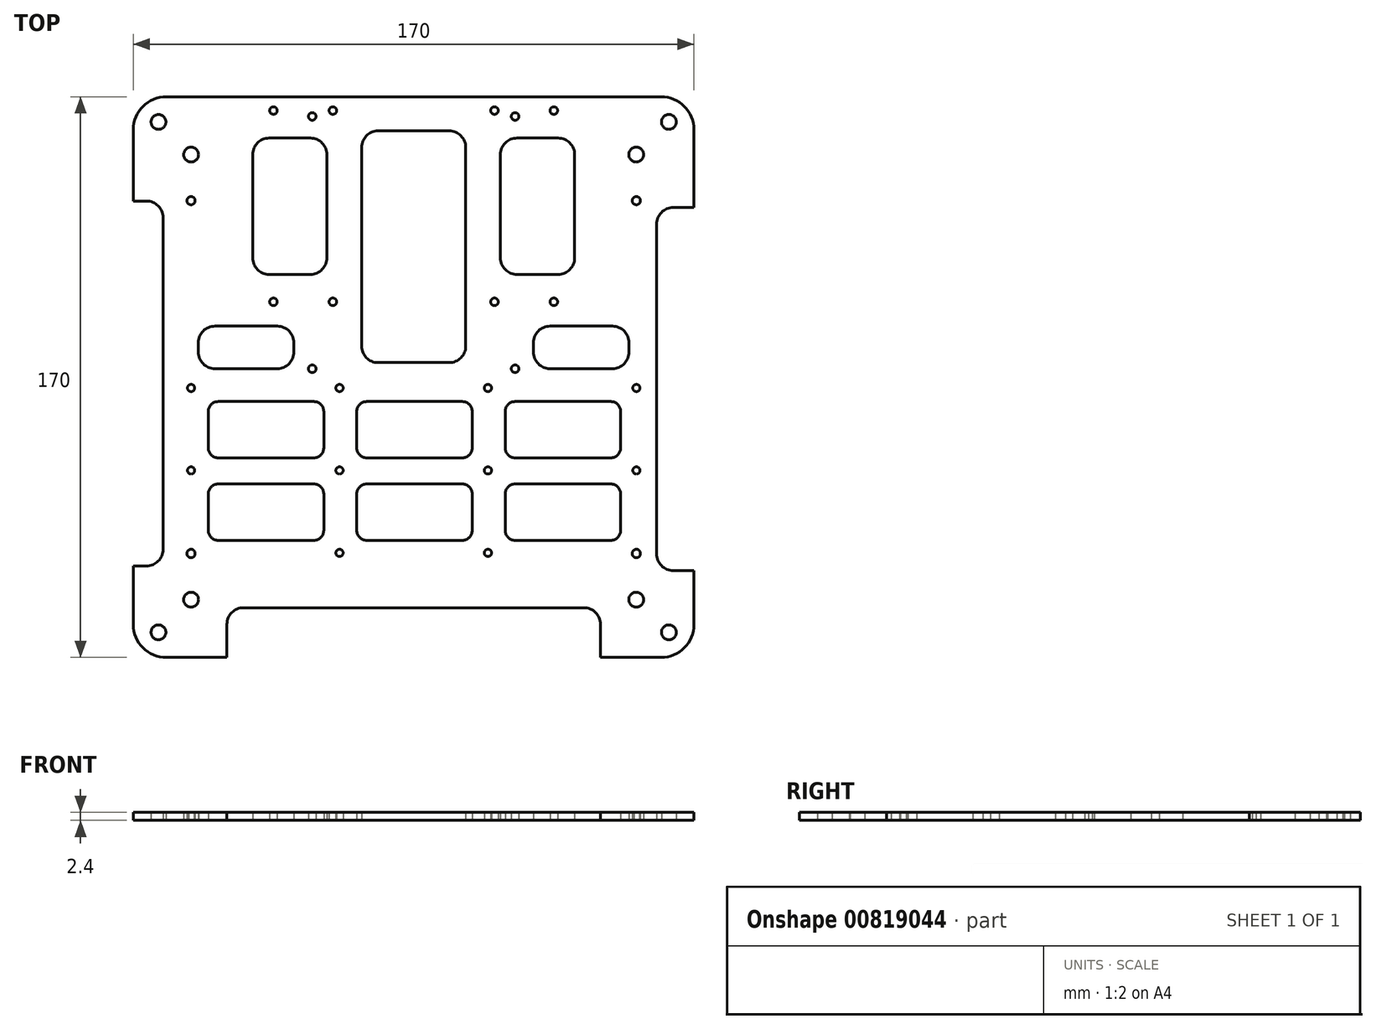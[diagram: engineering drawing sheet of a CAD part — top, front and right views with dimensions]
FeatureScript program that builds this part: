
annotation { "Feature Type Name" : "Feature", "Feature Type Description" : "" }
export const myFeature = defineFeature(function(context is Context, id is Id, definition is map)
    precondition{}
    {
        {
            var Q0;
            Q0=qCreatedBy(makeId("Top.planeOp"),FACE);
            var sketch = newSketch(context, id + "F0", { "sketchPlane" : qUnion([Q0])});
            skLineSegment(sketch, "E0.bottom", {"start": v(-100, -100) * mm, "end": v(100, -100) * mm, "construction": true});
            skLineSegment(sketch, "E0.top", {"start": v(-100, 100) * mm, "end": v(100, 100) * mm, "construction": true});
            skLineSegment(sketch, "E0.left", {"start": v(-100, -100) * mm, "end": v(-100, 100) * mm, "construction": true});
            skLineSegment(sketch, "E0.right", {"start": v(100, -100) * mm, "end": v(100, 100) * mm, "construction": true});
            skPoint(sketch, "E0.middle", {"position": v(0, 0) * mm});
            skCircle(sketch, "E1", {"center": v(-100, 100) * mm, "radius": 2.5 * mm, "construction": true});
            skCircle(sketch, "E2", {"center": v(100, 100) * mm, "radius": 2.5 * mm, "construction": true});
            skCircle(sketch, "E3", {"center": v(100, -100) * mm, "radius": 2.5 * mm, "construction": true});
            skCircle(sketch, "E4", {"center": v(-100, -100) * mm, "radius": 2.5 * mm, "construction": true});
            skLineSegment(sketch, "E5", {"start": v(-100, 100) * mm, "end": v(-77.37, 77.37) * mm, "construction": true});
            skLineSegment(sketch, "E6", {"start": v(-77.37, 77.37) * mm, "end": v(-67.47, 67.47) * mm, "construction": true});
            skCircle(sketch, "E7", {"center": v(-77.37, 77.37) * mm, "radius": 2.25 * mm});
            skCircle(sketch, "E8", {"center": v(-67.47, 67.47) * mm, "radius": 2.25 * mm});
            skLineSegment(sketch, "E9.bottom", {"start": v(-85, 85) * mm, "end": v(85, 85) * mm});
            skLineSegment(sketch, "E9.top", {"start": v(-85, -85) * mm, "end": v(85, -85) * mm});
            skLineSegment(sketch, "E9.left", {"start": v(-85, 85) * mm, "end": v(-85, -85) * mm});
            skLineSegment(sketch, "E9.right", {"start": v(85, 85) * mm, "end": v(85, -85) * mm});
            skLineSegment(sketch, "E10.bottom", {"start": v(-30.75, 2.54) * mm, "end": v(30.75, 2.54) * mm, "construction": true});
            skLineSegment(sketch, "E10.top", {"start": v(-30.75, 79.04) * mm, "end": v(30.75, 79.04) * mm, "construction": true});
            skLineSegment(sketch, "E10.left", {"start": v(-30.75, 2.54) * mm, "end": v(-30.75, 79.04) * mm, "construction": true});
            skLineSegment(sketch, "E10.right", {"start": v(30.75, 2.54) * mm, "end": v(30.75, 79.04) * mm, "construction": true});
            skPoint(sketch, "E10.middle", {"position": v(0, 40.8) * mm});
            skLineSegment(sketch, "E11.bottom", {"start": v(-35, -9.2) * mm, "end": v(35, -9.2) * mm, "construction": true});
            skLineSegment(sketch, "E11.top", {"start": v(-35, 90.8) * mm, "end": v(35, 90.8) * mm, "construction": true});
            skLineSegment(sketch, "E11.left", {"start": v(-35, -9.2) * mm, "end": v(-35, 90.8) * mm, "construction": true});
            skLineSegment(sketch, "E11.right", {"start": v(35, -9.2) * mm, "end": v(35, 90.8) * mm, "construction": true});
            skLineSegment(sketch, "E12.bottom", {"start": v(24.5, 22.83) * mm, "end": v(-24.5, 22.83) * mm, "construction": true});
            skLineSegment(sketch, "E12.top", {"start": v(24.5, 80.83) * mm, "end": v(-24.5, 80.83) * mm, "construction": true});
            skLineSegment(sketch, "E12.left", {"start": v(24.5, 22.83) * mm, "end": v(24.5, 80.83) * mm, "construction": true});
            skLineSegment(sketch, "E12.right", {"start": v(-24.5, 22.83) * mm, "end": v(-24.5, 80.83) * mm, "construction": true});
            skPoint(sketch, "E12.middle", {"position": v(0, 51.83) * mm});
            skLineSegment(sketch, "E13.bottom", {"start": v(28, 96.83) * mm, "end": v(-28, 96.83) * mm, "construction": true});
            skLineSegment(sketch, "E13.top", {"start": v(28, 6.83) * mm, "end": v(-28, 6.83) * mm, "construction": true});
            skLineSegment(sketch, "E13.left", {"start": v(28, 96.83) * mm, "end": v(28, 6.83) * mm, "construction": true});
            skLineSegment(sketch, "E13.right", {"start": v(-28, 96.83) * mm, "end": v(-28, 6.83) * mm, "construction": true});
            skLineSegment(sketch, "E14", {"start": v(0, 0) * mm, "end": v(0, 19) * mm, "construction": true});
            skLineSegment(sketch, "E15", {"start": v(0, 0) * mm, "end": v(16.24, 0) * mm, "construction": true});
            skCircle(sketch, "E16.MirrorC", {"center": v(77.37, 77.37) * mm, "radius": 2.25 * mm});
            skCircle(sketch, "E17.MirrorC", {"center": v(67.47, 67.47) * mm, "radius": 2.25 * mm});
            skCircle(sketch, "E18.MirrorC", {"center": v(-67.47, -67.47) * mm, "radius": 2.25 * mm});
            skCircle(sketch, "E19.MirrorC", {"center": v(-77.37, -77.37) * mm, "radius": 2.25 * mm});
            skCircle(sketch, "E20.MirrorC", {"center": v(77.37, -77.37) * mm, "radius": 2.25 * mm});
            skCircle(sketch, "E21.MirrorC", {"center": v(67.47, -67.47) * mm, "radius": 2.25 * mm});
            skCircle(sketch, "E22", {"center": v(-24.5, 80.83) * mm, "radius": 1.15 * mm});
            skCircle(sketch, "E23", {"center": v(24.5, 80.83) * mm, "radius": 1.15 * mm});
            skCircle(sketch, "E24", {"center": v(24.5, 22.83) * mm, "radius": 1.15 * mm});
            skCircle(sketch, "E25", {"center": v(-24.5, 22.83) * mm, "radius": 1.15 * mm});
            skCircle(sketch, "E26", {"center": v(-30.75, 79.04) * mm, "radius": 1.15 * mm});
            skCircle(sketch, "E27", {"center": v(30.75, 79.04) * mm, "radius": 1.15 * mm});
            skCircle(sketch, "E28", {"center": v(30.75, 2.54) * mm, "radius": 1.15 * mm});
            skCircle(sketch, "E29", {"center": v(-30.75, 2.54) * mm, "radius": 1.15 * mm});
            skLineSegment(sketch, "E30.bottom", {"start": v(-67.5, 53.5) * mm, "end": v(67.5, 53.5) * mm, "construction": true});
            skLineSegment(sketch, "E30.top", {"start": v(-67.5, -53.5) * mm, "end": v(67.5, -53.5) * mm, "construction": true});
            skLineSegment(sketch, "E30.left", {"start": v(-67.5, 53.5) * mm, "end": v(-67.5, -53.5) * mm, "construction": true});
            skLineSegment(sketch, "E30.right", {"start": v(67.5, 53.5) * mm, "end": v(67.5, -53.5) * mm, "construction": true});
            skCircle(sketch, "E31", {"center": v(-67.5, 53.5) * mm, "radius": 1.25 * mm});
            skCircle(sketch, "E32", {"center": v(67.5, 53.5) * mm, "radius": 1.25 * mm});
            skCircle(sketch, "E33", {"center": v(67.5, -53.5) * mm, "radius": 1.25 * mm});
            skCircle(sketch, "E34", {"center": v(-67.5, -53.5) * mm, "radius": 1.25 * mm});
            skLineSegment(sketch, "E35.bottom", {"start": v(-42.5, 22.83) * mm, "end": v(42.5, 22.83) * mm, "construction": true});
            skLineSegment(sketch, "E35.top", {"start": v(-42.5, 80.83) * mm, "end": v(42.5, 80.83) * mm, "construction": true});
            skLineSegment(sketch, "E35.left", {"start": v(-42.5, 22.83) * mm, "end": v(-42.5, 80.83) * mm, "construction": true});
            skLineSegment(sketch, "E35.right", {"start": v(42.5, 22.83) * mm, "end": v(42.5, 80.83) * mm, "construction": true});
            skCircle(sketch, "E36", {"center": v(-42.5, 80.83) * mm, "radius": 1.15 * mm});
            skCircle(sketch, "E37", {"center": v(-42.5, 22.83) * mm, "radius": 1.15 * mm});
            skCircle(sketch, "E38", {"center": v(42.5, 22.83) * mm, "radius": 1.15 * mm});
            skCircle(sketch, "E39", {"center": v(42.5, 80.83) * mm, "radius": 1.15 * mm});
            skSolve(sketch);
        }
        {
            var Q0;
            Q0=qSketchRegion(id+"F0",true);
            extrude(context, id + "F1", {"entities" : qUnion([Q0]), "depth" : 2.4 * mm, "offsetDistance" : 25 * mm});
        }
        {
            var Q0;
            Q0=makeQuery(id+"F1.opExtrude","SWEPT_EDGE",EDGE,{"disambiguationData":[OSD([sQuery(id+"F0.wireOp",EDGE,"E9.bottom"),sQuery(id+"F0.wireOp",EDGE,"E9.left")])]});
            var Q1;
            Q1=makeQuery(id+"F1.opExtrude","SWEPT_EDGE",EDGE,{"disambiguationData":[OSD([sQuery(id+"F0.wireOp",EDGE,"E9.bottom"),sQuery(id+"F0.wireOp",EDGE,"E9.right")])]});
            var Q2;
            Q2=makeQuery(id+"F1.opExtrude","SWEPT_EDGE",EDGE,{"disambiguationData":[OSD([sQuery(id+"F0.wireOp",EDGE,"E9.top"),sQuery(id+"F0.wireOp",EDGE,"E9.right")])]});
            var Q3;
            Q3=makeQuery(id+"F1.opExtrude","SWEPT_EDGE",EDGE,{"disambiguationData":[OSD([sQuery(id+"F0.wireOp",EDGE,"E9.top"),sQuery(id+"F0.wireOp",EDGE,"E9.left")])]});
            fillet(context, id + "F2", {"entities" : qUnion([Q0, Q1, Q2, Q3]), "radius" : 10 * mm, "tangentPropagation" : true, "allowEdgeOverflow" : false});
        }
        {
            var Q0;
            Q0=qCreatedBy(makeId("Top.planeOp"),FACE);
            var sketch = newSketch(context, id + "F3", { "sketchPlane" : qUnion([Q0])});
            skCircle(sketch, "E40", {"center": v(-67.48, -53.3) * mm, "radius": 1.1 * mm});
            skLineSegment(sketch, "E41", {"start": v(-67.48, -53.3) * mm, "end": v(-67.48, -28.3) * mm, "construction": true});
            skCircle(sketch, "E42", {"center": v(-67.48, -28.3) * mm, "radius": 1.1 * mm});
            skLineSegment(sketch, "E43.bottom", {"start": v(-59.25, -32.4) * mm, "end": v(-30.25, -32.4) * mm});
            skLineSegment(sketch, "E43.top", {"start": v(-59.25, -49.48) * mm, "end": v(-30.25, -49.48) * mm});
            skLineSegment(sketch, "E43.left", {"start": v(-62.25, -35.4) * mm, "end": v(-62.25, -46.48) * mm});
            skLineSegment(sketch, "E43.right", {"start": v(-27.25, -35.4) * mm, "end": v(-27.25, -46.48) * mm});
            skPoint(sketch, "E44.visualSharp", {"position": v(-62.25, -32.4) * mm});
            skArc(sketch, "E44.filletArc", {"start": v(-59.25, -32.4) * mm, "mid": v(-61.37, -33.29) * mm, "end": v(-62.25, -35.4) * mm});
            skPoint(sketch, "E45.visualSharp", {"position": v(-27.25, -32.4) * mm});
            skArc(sketch, "E45.filletArc", {"start": v(-27.25, -35.4) * mm, "mid": v(-28.13, -33.29) * mm, "end": v(-30.25, -32.4) * mm});
            skPoint(sketch, "E46.visualSharp", {"position": v(-27.25, -49.48) * mm});
            skArc(sketch, "E46.filletArc", {"start": v(-30.25, -49.48) * mm, "mid": v(-28.13, -48.6) * mm, "end": v(-27.25, -46.48) * mm});
            skPoint(sketch, "E47.visualSharp", {"position": v(-62.25, -49.48) * mm});
            skArc(sketch, "E47.filletArc", {"start": v(-62.25, -46.48) * mm, "mid": v(-61.37, -48.6) * mm, "end": v(-59.25, -49.48) * mm});
            skLineSegment(sketch, "E48.0.1.0", {"start": v(-27.25, -10.4) * mm, "end": v(-27.25, -21.48) * mm});
            skLineSegment(sketch, "E48.0.1.1", {"start": v(-59.25, -7.4) * mm, "end": v(-30.25, -7.4) * mm});
            skLineSegment(sketch, "E48.0.1.2", {"start": v(-67.48, -28.3) * mm, "end": v(-67.48, -3.3) * mm, "construction": true});
            skLineSegment(sketch, "E48.0.1.3", {"start": v(-62.25, -10.4) * mm, "end": v(-62.25, -21.48) * mm});
            skLineSegment(sketch, "E48.0.1.4", {"start": v(-59.25, -24.48) * mm, "end": v(-30.25, -24.48) * mm});
            skPoint(sketch, "E48.0.1.5", {"position": v(-62.25, -24.48) * mm});
            skPoint(sketch, "E48.0.1.6", {"position": v(-27.25, -24.48) * mm});
            skPoint(sketch, "E48.0.1.7", {"position": v(-27.25, -7.4) * mm});
            skPoint(sketch, "E48.0.1.8", {"position": v(-62.25, -7.4) * mm});
            skArc(sketch, "E48.0.1.9", {"start": v(-59.25, -7.4) * mm, "mid": v(-61.37, -8.29) * mm, "end": v(-62.25, -10.4) * mm});
            skArc(sketch, "E48.0.1.10", {"start": v(-30.25, -24.48) * mm, "mid": v(-28.13, -23.6) * mm, "end": v(-27.25, -21.48) * mm});
            skArc(sketch, "E48.0.1.11", {"start": v(-62.25, -21.48) * mm, "mid": v(-61.37, -23.6) * mm, "end": v(-59.25, -24.48) * mm});
            skCircle(sketch, "E48.0.1.12", {"center": v(-67.48, -3.3) * mm, "radius": 1.1 * mm});
            skArc(sketch, "E48.0.1.14", {"start": v(-27.25, -10.4) * mm, "mid": v(-28.13, -8.29) * mm, "end": v(-30.25, -7.4) * mm});
            skLineSegment(sketch, "E48.1.0.0", {"start": v(17.75, -35.4) * mm, "end": v(17.75, -46.48) * mm});
            skLineSegment(sketch, "E48.1.0.1", {"start": v(-14.25, -32.4) * mm, "end": v(14.75, -32.4) * mm});
            skLineSegment(sketch, "E48.1.0.2", {"start": v(-22.48, -53.3) * mm, "end": v(-22.48, -28.3) * mm, "construction": true});
            skLineSegment(sketch, "E48.1.0.3", {"start": v(-17.25, -35.4) * mm, "end": v(-17.25, -46.48) * mm});
            skLineSegment(sketch, "E48.1.0.4", {"start": v(-14.25, -49.48) * mm, "end": v(14.75, -49.48) * mm});
            skPoint(sketch, "E48.1.0.5", {"position": v(-17.25, -49.48) * mm});
            skPoint(sketch, "E48.1.0.6", {"position": v(17.75, -49.48) * mm});
            skPoint(sketch, "E48.1.0.7", {"position": v(17.75, -32.4) * mm});
            skPoint(sketch, "E48.1.0.8", {"position": v(-17.25, -32.4) * mm});
            skArc(sketch, "E48.1.0.9", {"start": v(-14.25, -32.4) * mm, "mid": v(-16.37, -33.29) * mm, "end": v(-17.25, -35.4) * mm});
            skArc(sketch, "E48.1.0.10", {"start": v(14.75, -49.48) * mm, "mid": v(16.87, -48.6) * mm, "end": v(17.75, -46.48) * mm});
            skArc(sketch, "E48.1.0.11", {"start": v(-17.25, -46.48) * mm, "mid": v(-16.37, -48.6) * mm, "end": v(-14.25, -49.48) * mm});
            skCircle(sketch, "E48.1.0.12", {"center": v(-22.48, -28.3) * mm, "radius": 1.1 * mm});
            skCircle(sketch, "E48.1.0.13", {"center": v(-22.48, -53.3) * mm, "radius": 1.1 * mm});
            skArc(sketch, "E48.1.0.14", {"start": v(17.75, -35.4) * mm, "mid": v(16.87, -33.29) * mm, "end": v(14.75, -32.4) * mm});
            skLineSegment(sketch, "E48.1.1.0", {"start": v(17.75, -10.4) * mm, "end": v(17.75, -21.48) * mm});
            skLineSegment(sketch, "E48.1.1.1", {"start": v(-14.25, -7.4) * mm, "end": v(14.75, -7.4) * mm});
            skLineSegment(sketch, "E48.1.1.2", {"start": v(-22.48, -28.3) * mm, "end": v(-22.48, -3.3) * mm, "construction": true});
            skLineSegment(sketch, "E48.1.1.3", {"start": v(-17.25, -10.4) * mm, "end": v(-17.25, -21.48) * mm});
            skLineSegment(sketch, "E48.1.1.4", {"start": v(-14.25, -24.48) * mm, "end": v(14.75, -24.48) * mm});
            skPoint(sketch, "E48.1.1.5", {"position": v(-17.25, -24.48) * mm});
            skPoint(sketch, "E48.1.1.6", {"position": v(17.75, -24.48) * mm});
            skPoint(sketch, "E48.1.1.7", {"position": v(17.75, -7.4) * mm});
            skPoint(sketch, "E48.1.1.8", {"position": v(-17.25, -7.4) * mm});
            skArc(sketch, "E48.1.1.9", {"start": v(-14.25, -7.4) * mm, "mid": v(-16.37, -8.29) * mm, "end": v(-17.25, -10.4) * mm});
            skArc(sketch, "E48.1.1.10", {"start": v(14.75, -24.48) * mm, "mid": v(16.87, -23.6) * mm, "end": v(17.75, -21.48) * mm});
            skArc(sketch, "E48.1.1.11", {"start": v(-17.25, -21.48) * mm, "mid": v(-16.37, -23.6) * mm, "end": v(-14.25, -24.48) * mm});
            skCircle(sketch, "E48.1.1.12", {"center": v(-22.48, -3.3) * mm, "radius": 1.1 * mm});
            skCircle(sketch, "E48.1.1.13", {"center": v(-22.48, -28.3) * mm, "radius": 1.1 * mm});
            skArc(sketch, "E48.1.1.14", {"start": v(17.75, -10.4) * mm, "mid": v(16.87, -8.29) * mm, "end": v(14.75, -7.4) * mm});
            skLineSegment(sketch, "E48.2.0.0", {"start": v(62.75, -35.4) * mm, "end": v(62.75, -46.48) * mm});
            skLineSegment(sketch, "E48.2.0.1", {"start": v(30.75, -32.4) * mm, "end": v(59.75, -32.4) * mm});
            skLineSegment(sketch, "E48.2.0.2", {"start": v(22.52, -53.3) * mm, "end": v(22.52, -28.3) * mm, "construction": true});
            skLineSegment(sketch, "E48.2.0.3", {"start": v(27.75, -35.4) * mm, "end": v(27.75, -46.48) * mm});
            skLineSegment(sketch, "E48.2.0.4", {"start": v(30.75, -49.48) * mm, "end": v(59.75, -49.48) * mm});
            skPoint(sketch, "E48.2.0.5", {"position": v(27.75, -49.48) * mm});
            skPoint(sketch, "E48.2.0.6", {"position": v(62.75, -49.48) * mm});
            skPoint(sketch, "E48.2.0.7", {"position": v(62.75, -32.4) * mm});
            skPoint(sketch, "E48.2.0.8", {"position": v(27.75, -32.4) * mm});
            skArc(sketch, "E48.2.0.9", {"start": v(30.75, -32.4) * mm, "mid": v(28.63, -33.29) * mm, "end": v(27.75, -35.4) * mm});
            skArc(sketch, "E48.2.0.10", {"start": v(59.75, -49.48) * mm, "mid": v(61.87, -48.6) * mm, "end": v(62.75, -46.48) * mm});
            skArc(sketch, "E48.2.0.11", {"start": v(27.75, -46.48) * mm, "mid": v(28.63, -48.6) * mm, "end": v(30.75, -49.48) * mm});
            skCircle(sketch, "E48.2.0.12", {"center": v(22.52, -28.3) * mm, "radius": 1.1 * mm});
            skCircle(sketch, "E48.2.0.13", {"center": v(22.52, -53.3) * mm, "radius": 1.1 * mm});
            skArc(sketch, "E48.2.0.14", {"start": v(62.75, -35.4) * mm, "mid": v(61.87, -33.29) * mm, "end": v(59.75, -32.4) * mm});
            skLineSegment(sketch, "E48.2.1.0", {"start": v(62.75, -10.4) * mm, "end": v(62.75, -21.48) * mm});
            skLineSegment(sketch, "E48.2.1.1", {"start": v(30.75, -7.4) * mm, "end": v(59.75, -7.4) * mm});
            skLineSegment(sketch, "E48.2.1.2", {"start": v(22.52, -28.3) * mm, "end": v(22.52, -3.3) * mm, "construction": true});
            skLineSegment(sketch, "E48.2.1.3", {"start": v(27.75, -10.4) * mm, "end": v(27.75, -21.48) * mm});
            skLineSegment(sketch, "E48.2.1.4", {"start": v(30.75, -24.48) * mm, "end": v(59.75, -24.48) * mm});
            skPoint(sketch, "E48.2.1.5", {"position": v(27.75, -24.48) * mm});
            skPoint(sketch, "E48.2.1.6", {"position": v(62.75, -24.48) * mm});
            skPoint(sketch, "E48.2.1.7", {"position": v(62.75, -7.4) * mm});
            skPoint(sketch, "E48.2.1.8", {"position": v(27.75, -7.4) * mm});
            skArc(sketch, "E48.2.1.9", {"start": v(30.75, -7.4) * mm, "mid": v(28.63, -8.29) * mm, "end": v(27.75, -10.4) * mm});
            skArc(sketch, "E48.2.1.10", {"start": v(59.75, -24.48) * mm, "mid": v(61.87, -23.6) * mm, "end": v(62.75, -21.48) * mm});
            skArc(sketch, "E48.2.1.11", {"start": v(27.75, -21.48) * mm, "mid": v(28.63, -23.6) * mm, "end": v(30.75, -24.48) * mm});
            skCircle(sketch, "E48.2.1.12", {"center": v(22.52, -3.3) * mm, "radius": 1.1 * mm});
            skCircle(sketch, "E48.2.1.13", {"center": v(22.52, -28.3) * mm, "radius": 1.1 * mm});
            skArc(sketch, "E48.2.1.14", {"start": v(62.75, -10.4) * mm, "mid": v(61.87, -8.29) * mm, "end": v(59.75, -7.4) * mm});
            skLineSegment(sketch, "E48.3.0.0", {"start": v(107.75, -35.4) * mm, "end": v(107.75, -46.48) * mm, "construction": true});
            skLineSegment(sketch, "E48.3.0.1", {"start": v(75.75, -32.4) * mm, "end": v(104.75, -32.4) * mm, "construction": true});
            skLineSegment(sketch, "E48.3.0.2", {"start": v(67.52, -53.3) * mm, "end": v(67.52, -28.3) * mm, "construction": true});
            skLineSegment(sketch, "E48.3.0.3", {"start": v(72.75, -35.4) * mm, "end": v(72.75, -46.48) * mm, "construction": true});
            skLineSegment(sketch, "E48.3.0.4", {"start": v(75.75, -49.48) * mm, "end": v(104.75, -49.48) * mm, "construction": true});
            skPoint(sketch, "E48.3.0.5", {"position": v(72.75, -49.48) * mm});
            skPoint(sketch, "E48.3.0.6", {"position": v(107.75, -49.48) * mm});
            skPoint(sketch, "E48.3.0.7", {"position": v(107.75, -32.4) * mm});
            skPoint(sketch, "E48.3.0.8", {"position": v(72.75, -32.4) * mm});
            skArc(sketch, "E48.3.0.9", {"start": v(75.75, -32.4) * mm, "mid": v(73.63, -33.29) * mm, "end": v(72.75, -35.4) * mm, "construction": true});
            skArc(sketch, "E48.3.0.10", {"start": v(104.75, -49.48) * mm, "mid": v(106.87, -48.6) * mm, "end": v(107.75, -46.48) * mm, "construction": true});
            skArc(sketch, "E48.3.0.11", {"start": v(72.75, -46.48) * mm, "mid": v(73.63, -48.6) * mm, "end": v(75.75, -49.48) * mm, "construction": true});
            skCircle(sketch, "E48.3.0.12", {"center": v(67.52, -28.3) * mm, "radius": 1.1 * mm});
            skCircle(sketch, "E48.3.0.13", {"center": v(67.52, -53.3) * mm, "radius": 1.1 * mm});
            skArc(sketch, "E48.3.0.14", {"start": v(107.75, -35.4) * mm, "mid": v(106.87, -33.29) * mm, "end": v(104.75, -32.4) * mm, "construction": true});
            skLineSegment(sketch, "E48.3.1.0", {"start": v(107.75, -10.4) * mm, "end": v(107.75, -21.48) * mm, "construction": true});
            skLineSegment(sketch, "E48.3.1.1", {"start": v(75.75, -7.4) * mm, "end": v(104.75, -7.4) * mm, "construction": true});
            skLineSegment(sketch, "E48.3.1.2", {"start": v(67.52, -28.3) * mm, "end": v(67.52, -3.3) * mm, "construction": true});
            skLineSegment(sketch, "E48.3.1.3", {"start": v(72.75, -10.4) * mm, "end": v(72.75, -21.48) * mm, "construction": true});
            skLineSegment(sketch, "E48.3.1.4", {"start": v(75.75, -24.48) * mm, "end": v(104.75, -24.48) * mm, "construction": true});
            skPoint(sketch, "E48.3.1.5", {"position": v(72.75, -24.48) * mm});
            skPoint(sketch, "E48.3.1.6", {"position": v(107.75, -24.48) * mm});
            skPoint(sketch, "E48.3.1.7", {"position": v(107.75, -7.4) * mm});
            skPoint(sketch, "E48.3.1.8", {"position": v(72.75, -7.4) * mm});
            skArc(sketch, "E48.3.1.9", {"start": v(75.75, -7.4) * mm, "mid": v(73.63, -8.29) * mm, "end": v(72.75, -10.4) * mm, "construction": true});
            skArc(sketch, "E48.3.1.10", {"start": v(104.75, -24.48) * mm, "mid": v(106.87, -23.6) * mm, "end": v(107.75, -21.48) * mm, "construction": true});
            skArc(sketch, "E48.3.1.11", {"start": v(72.75, -21.48) * mm, "mid": v(73.63, -23.6) * mm, "end": v(75.75, -24.48) * mm, "construction": true});
            skCircle(sketch, "E48.3.1.12", {"center": v(67.52, -3.3) * mm, "radius": 1.1 * mm});
            skCircle(sketch, "E48.3.1.13", {"center": v(67.52, -28.3) * mm, "radius": 1.1 * mm});
            skArc(sketch, "E48.3.1.14", {"start": v(107.75, -10.4) * mm, "mid": v(106.87, -8.29) * mm, "end": v(104.75, -7.4) * mm, "construction": true});
            skLineSegment(sketch, "E48.direction1", {"start": v(-67.48, -53.3) * mm, "end": v(-22.48, -53.3) * mm, "construction": true});
            skLineSegment(sketch, "E49.bottom", {"start": v(-81, 53.4) * mm, "end": v(-120.52, 53.4) * mm});
            skLineSegment(sketch, "E49.top", {"start": v(-81, -57.25) * mm, "end": v(-120.52, -57.25) * mm});
            skLineSegment(sketch, "E49.left", {"start": v(-76, 48.4) * mm, "end": v(-76, -52.25) * mm});
            skLineSegment(sketch, "E49.right", {"start": v(-120.52, 53.4) * mm, "end": v(-120.52, -57.25) * mm});
            skPoint(sketch, "E49.middle", {"position": v(-98.26, -1.93) * mm});
            skLineSegment(sketch, "E50.bottom", {"start": v(78.67, 51.4) * mm, "end": v(100.25, 51.4) * mm});
            skLineSegment(sketch, "E50.top", {"start": v(78.67, -58.63) * mm, "end": v(100.25, -58.63) * mm});
            skLineSegment(sketch, "E50.left", {"start": v(73.67, 46.4) * mm, "end": v(73.67, -53.63) * mm});
            skLineSegment(sketch, "E50.right", {"start": v(100.25, 51.4) * mm, "end": v(100.25, -58.63) * mm});
            skPoint(sketch, "E50.middle", {"position": v(86.96, -3.6) * mm});
            skPoint(sketch, "E51.visualSharp", {"position": v(73.67, 51.4) * mm});
            skArc(sketch, "E51.filletArc", {"start": v(78.67, 51.4) * mm, "mid": v(75.13, 49.94) * mm, "end": v(73.67, 46.4) * mm});
            skPoint(sketch, "E52.visualSharp", {"position": v(73.67, -58.63) * mm});
            skArc(sketch, "E52.filletArc", {"start": v(73.67, -53.63) * mm, "mid": v(75.13, -57.16) * mm, "end": v(78.67, -58.63) * mm});
            skArc(sketch, "E53.filletArc", {"start": v(-76, 48.4) * mm, "mid": v(-77.46, 51.93) * mm, "end": v(-81, 53.4) * mm});
            skPoint(sketch, "E54.visualSharp", {"position": v(-76, -57.25) * mm});
            skArc(sketch, "E54.filletArc", {"start": v(-81, -57.25) * mm, "mid": v(-77.46, -55.79) * mm, "end": v(-76, -52.25) * mm});
            skLineSegment(sketch, "E55.bottom", {"start": v(56.61, -107.65) * mm, "end": v(-56.61, -107.65) * mm});
            skLineSegment(sketch, "E55.top", {"start": v(51.61, -69.91) * mm, "end": v(-51.61, -69.91) * mm});
            skLineSegment(sketch, "E55.left", {"start": v(56.61, -107.65) * mm, "end": v(56.61, -74.91) * mm});
            skLineSegment(sketch, "E55.right", {"start": v(-56.61, -107.65) * mm, "end": v(-56.61, -74.91) * mm});
            skPoint(sketch, "E55.middle", {"position": v(0, -88.78) * mm});
            skPoint(sketch, "E56.visualSharp", {"position": v(-56.61, -69.91) * mm});
            skArc(sketch, "E56.filletArc", {"start": v(-51.61, -69.91) * mm, "mid": v(-55.15, -71.38) * mm, "end": v(-56.61, -74.91) * mm});
            skPoint(sketch, "E57.visualSharp", {"position": v(56.61, -69.91) * mm});
            skArc(sketch, "E57.filletArc", {"start": v(56.61, -74.91) * mm, "mid": v(55.15, -71.38) * mm, "end": v(51.61, -69.91) * mm});
            skLineSegment(sketch, "E58.bottom", {"start": v(-10.79, 74.66) * mm, "end": v(10.79, 74.66) * mm});
            skLineSegment(sketch, "E58.top", {"start": v(-10.79, 4.4) * mm, "end": v(10.79, 4.4) * mm});
            skLineSegment(sketch, "E58.left", {"start": v(-15.79, 69.66) * mm, "end": v(-15.79, 9.4) * mm});
            skLineSegment(sketch, "E58.right", {"start": v(15.79, 69.66) * mm, "end": v(15.79, 9.4) * mm});
            skPoint(sketch, "E58.middle", {"position": v(0, 39.53) * mm});
            skLineSegment(sketch, "E59.bottom", {"start": v(-43.81, 31.16) * mm, "end": v(-31.31, 31.16) * mm});
            skLineSegment(sketch, "E59.top", {"start": v(-43.81, 72.49) * mm, "end": v(-31.31, 72.49) * mm});
            skLineSegment(sketch, "E59.left", {"start": v(-48.81, 36.16) * mm, "end": v(-48.81, 67.49) * mm});
            skLineSegment(sketch, "E59.right", {"start": v(-26.31, 36.16) * mm, "end": v(-26.31, 67.49) * mm});
            skPoint(sketch, "E59.middle", {"position": v(-37.56, 51.82) * mm});
            skLineSegment(sketch, "E60", {"start": v(0, 0) * mm, "end": v(0, 21.62) * mm, "construction": true});
            skLineSegment(sketch, "E61.MirrorCS", {"start": v(26.31, 36.16) * mm, "end": v(26.31, 67.49) * mm});
            skPoint(sketch, "E62.MirrorP", {"position": v(37.56, 51.82) * mm});
            skLineSegment(sketch, "E63.MirrorCS", {"start": v(43.81, 31.16) * mm, "end": v(31.31, 31.16) * mm});
            skLineSegment(sketch, "E64.MirrorCS", {"start": v(43.81, 72.49) * mm, "end": v(31.31, 72.49) * mm});
            skLineSegment(sketch, "E65.MirrorCS", {"start": v(48.81, 36.16) * mm, "end": v(48.81, 67.49) * mm});
            skPoint(sketch, "E66.visualSharp", {"position": v(-48.81, 72.49) * mm});
            skArc(sketch, "E66.filletArc", {"start": v(-43.81, 72.49) * mm, "mid": v(-47.35, 71.02) * mm, "end": v(-48.81, 67.49) * mm});
            skPoint(sketch, "E67.visualSharp", {"position": v(-26.31, 72.49) * mm});
            skArc(sketch, "E67.filletArc", {"start": v(-26.31, 67.49) * mm, "mid": v(-27.78, 71.02) * mm, "end": v(-31.31, 72.49) * mm});
            skPoint(sketch, "E68.visualSharp", {"position": v(-26.31, 31.16) * mm});
            skArc(sketch, "E68.filletArc", {"start": v(-31.31, 31.16) * mm, "mid": v(-27.78, 32.62) * mm, "end": v(-26.31, 36.16) * mm});
            skPoint(sketch, "E69.visualSharp", {"position": v(-48.81, 31.16) * mm});
            skArc(sketch, "E69.filletArc", {"start": v(-48.81, 36.16) * mm, "mid": v(-47.35, 32.62) * mm, "end": v(-43.81, 31.16) * mm});
            skPoint(sketch, "E70.visualSharp", {"position": v(26.31, 31.16) * mm});
            skArc(sketch, "E70.filletArc", {"start": v(26.31, 36.16) * mm, "mid": v(27.78, 32.62) * mm, "end": v(31.31, 31.16) * mm});
            skPoint(sketch, "E71.visualSharp", {"position": v(48.81, 31.16) * mm});
            skArc(sketch, "E71.filletArc", {"start": v(43.81, 31.16) * mm, "mid": v(47.35, 32.62) * mm, "end": v(48.81, 36.16) * mm});
            skPoint(sketch, "E72.visualSharp", {"position": v(48.81, 72.49) * mm});
            skArc(sketch, "E72.filletArc", {"start": v(48.81, 67.49) * mm, "mid": v(47.35, 71.02) * mm, "end": v(43.81, 72.49) * mm});
            skPoint(sketch, "E73.visualSharp", {"position": v(26.31, 72.49) * mm});
            skArc(sketch, "E73.filletArc", {"start": v(31.31, 72.49) * mm, "mid": v(27.78, 71.02) * mm, "end": v(26.31, 67.49) * mm});
            skPoint(sketch, "E74.visualSharp", {"position": v(15.79, 4.4) * mm});
            skArc(sketch, "E74.filletArc", {"start": v(10.79, 4.4) * mm, "mid": v(14.32, 5.86) * mm, "end": v(15.79, 9.4) * mm});
            skPoint(sketch, "E75.visualSharp", {"position": v(15.79, 74.66) * mm});
            skArc(sketch, "E75.filletArc", {"start": v(15.79, 69.66) * mm, "mid": v(14.32, 73.2) * mm, "end": v(10.79, 74.66) * mm});
            skPoint(sketch, "E76.visualSharp", {"position": v(-15.79, 74.66) * mm});
            skArc(sketch, "E76.filletArc", {"start": v(-10.79, 74.66) * mm, "mid": v(-14.32, 73.2) * mm, "end": v(-15.79, 69.66) * mm});
            skPoint(sketch, "E77.visualSharp", {"position": v(-15.79, 4.4) * mm});
            skArc(sketch, "E77.filletArc", {"start": v(-15.79, 9.4) * mm, "mid": v(-14.32, 5.86) * mm, "end": v(-10.79, 4.4) * mm});
            skLineSegment(sketch, "E78.bottom", {"start": v(-41.33, 2.58) * mm, "end": v(-60.27, 2.58) * mm});
            skLineSegment(sketch, "E78.top", {"start": v(-41.33, 15.45) * mm, "end": v(-60.27, 15.45) * mm});
            skLineSegment(sketch, "E78.left", {"start": v(-36.33, 7.58) * mm, "end": v(-36.33, 10.45) * mm});
            skLineSegment(sketch, "E78.right", {"start": v(-65.27, 7.58) * mm, "end": v(-65.27, 10.45) * mm});
            skPoint(sketch, "E78.middle", {"position": v(-50.8, 9.01) * mm});
            skPoint(sketch, "E79.visualSharp", {"position": v(-65.27, 15.45) * mm});
            skArc(sketch, "E79.filletArc", {"start": v(-60.27, 15.45) * mm, "mid": v(-63.8, 13.98) * mm, "end": v(-65.27, 10.45) * mm});
            skPoint(sketch, "E80.visualSharp", {"position": v(-36.33, 15.45) * mm});
            skArc(sketch, "E80.filletArc", {"start": v(-36.33, 10.45) * mm, "mid": v(-37.8, 13.98) * mm, "end": v(-41.33, 15.45) * mm});
            skPoint(sketch, "E81.visualSharp", {"position": v(-65.27, 2.58) * mm});
            skArc(sketch, "E81.filletArc", {"start": v(-65.27, 7.58) * mm, "mid": v(-63.8, 4.04) * mm, "end": v(-60.27, 2.58) * mm});
            skPoint(sketch, "E82.visualSharp", {"position": v(-36.33, 2.58) * mm});
            skArc(sketch, "E82.filletArc", {"start": v(-41.33, 2.58) * mm, "mid": v(-37.8, 4.04) * mm, "end": v(-36.33, 7.58) * mm});
            skArc(sketch, "E83.MirrorCS", {"start": v(65.27, 7.58) * mm, "mid": v(63.8, 4.04) * mm, "end": v(60.27, 2.58) * mm});
            skArc(sketch, "E84.MirrorCS", {"start": v(36.33, 10.45) * mm, "mid": v(37.8, 13.98) * mm, "end": v(41.33, 15.45) * mm});
            skArc(sketch, "E85.MirrorCS", {"start": v(60.27, 15.45) * mm, "mid": v(63.8, 13.98) * mm, "end": v(65.27, 10.45) * mm});
            skArc(sketch, "E86.MirrorCS", {"start": v(41.33, 2.58) * mm, "mid": v(37.8, 4.04) * mm, "end": v(36.33, 7.58) * mm});
            skPoint(sketch, "E87.MirrorP", {"position": v(65.27, 2.58) * mm});
            skPoint(sketch, "E88.MirrorP", {"position": v(36.33, 2.58) * mm});
            skPoint(sketch, "E89.MirrorP", {"position": v(36.33, 15.45) * mm});
            skLineSegment(sketch, "E90.MirrorCS", {"start": v(41.33, 2.58) * mm, "end": v(60.27, 2.58) * mm});
            skLineSegment(sketch, "E91.MirrorCS", {"start": v(41.33, 15.45) * mm, "end": v(60.27, 15.45) * mm});
            skPoint(sketch, "E92.MirrorP", {"position": v(65.27, 15.45) * mm});
            skLineSegment(sketch, "E93.MirrorCS", {"start": v(36.33, 7.58) * mm, "end": v(36.33, 10.45) * mm});
            skLineSegment(sketch, "E94.MirrorCS", {"start": v(65.27, 7.58) * mm, "end": v(65.27, 10.45) * mm});
            skPoint(sketch, "E95.MirrorP", {"position": v(50.8, 9.01) * mm});
            skSolve(sketch);
        }
        {
            var Q0;
            Q0=qSketchRegion(id+"F3",true);
            extrude(context, id + "F4", {"entities" : qUnion([Q0]), "operationType" : NewBodyOperationType.REMOVE, "depth" : 25 * mm, "offsetDistance" : 25 * mm});
        }
    });
